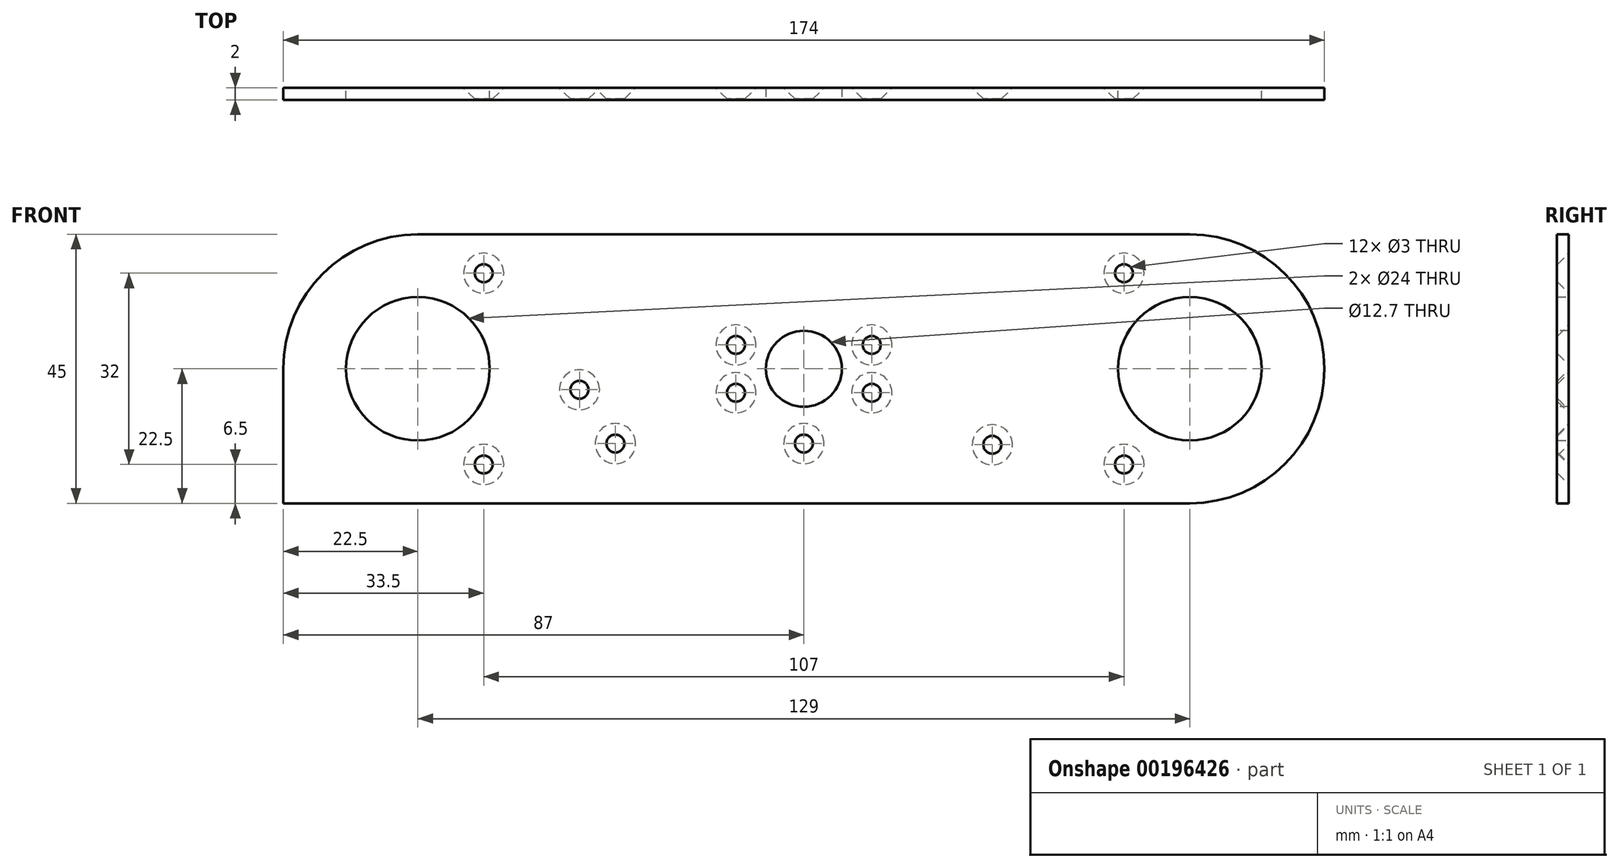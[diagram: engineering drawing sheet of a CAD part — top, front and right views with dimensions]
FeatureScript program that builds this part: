
annotation { "Feature Type Name" : "Feature", "Feature Type Description" : "" }
export const myFeature = defineFeature(function(context is Context, id is Id, definition is map)
    precondition{}
    {
        {
            var Q0;
            Q0=qCreatedBy(makeId("Front.planeOp"),FACE);
            var sketch = newSketch(context, id + "F0", { "sketchPlane" : qUnion([Q0])});
            skLineSegment(sketch, "E0.bottom", {"start": v(64.5, 22.5) * mm, "end": v(-64.5, 22.5) * mm});
            skLineSegment(sketch, "E0.top", {"start": v(64.5, -22.5) * mm, "end": v(-64.5, -22.5) * mm});
            skPoint(sketch, "E0.middle", {"position": v(0, 0) * mm});
            skCircle(sketch, "E1", {"center": v(64.5, 0) * mm, "radius": 12 * mm});
            skCircle(sketch, "E2", {"center": v(-64.5, 0) * mm, "radius": 12 * mm});
            skArc(sketch, "E3", {"start": v(-64.5, 22.5) * mm, "mid": v(-87, 0) * mm, "end": v(-64.5, -22.5) * mm});
            skArc(sketch, "E4", {"start": v(64.5, -22.5) * mm, "mid": v(87, 0) * mm, "end": v(64.5, 22.5) * mm});
            skPoint(sketch, "E5.orphan", {"position": v(-81.5, 22.5) * mm});
            skPoint(sketch, "E6.orphan", {"position": v(-81.5, -22.5) * mm});
            skPoint(sketch, "E7.orphan", {"position": v(81.5, 22.5) * mm});
            skPoint(sketch, "E8.orphan", {"position": v(81.5, -22.5) * mm});
            skSolve(sketch);
        }
        {
            var Q0;
            Q0=qSketchRegion(id+"F0",true);
            extrude(context, id + "F1", {"entities" : qUnion([Q0]), "depth" : 2 * mm, "offsetDistance" : 25 * mm});
        }
        {
            var Q0;
            Q0=makeQuery(id+"F1.opExtrude","CAP_FACE",FACE,{"disambiguationData":[OSD([sQuery(id+"F0.wireOp",EDGE,"E0.bottom"),sQuery(id+"F0.wireOp",EDGE,"E0.top"),sQuery(id+"F0.wireOp",EDGE,"E1"),sQuery(id+"F0.wireOp",EDGE,"E2"),sQuery(id+"F0.wireOp",EDGE,"E3"),sQuery(id+"F0.wireOp",EDGE,"E4")])],"isStart":false});
            var sketch = newSketch(context, id + "F2", { "sketchPlane" : qUnion([Q0])});
            skLineSegment(sketch, "E9.top", {"start": v(-64.5, -22.5) * mm, "end": v(-87, -22.5) * mm});
            skLineSegment(sketch, "E9.right", {"start": v(-87, 0) * mm, "end": v(-87, -22.5) * mm});
            skPoint(sketch, "E9.left.start.orphan", {"position": v(-64.5, 0) * mm});
            skLineSegment(sketch, "E10", {"start": v(-87, 0) * mm, "end": v(-80.88, 0) * mm});
            skLineSegment(sketch, "E11", {"start": v(-80.88, 0) * mm, "end": v(-78.27, -9.46) * mm});
            skLineSegment(sketch, "E12", {"start": v(-78.27, -9.46) * mm, "end": v(-70.55, -14.76) * mm});
            skLineSegment(sketch, "E13", {"start": v(-70.55, -14.76) * mm, "end": v(-64.5, -17.43) * mm});
            skLineSegment(sketch, "E14", {"start": v(-64.5, -17.43) * mm, "end": v(-64.5, -22.5) * mm});
            skSolve(sketch);
        }
        {
            var Q0;
            Q0=qSketchRegion(id+"F2",true);
            extrude(context, id + "F3", {"entities" : qUnion([Q0]), "operationType" : NewBodyOperationType.ADD, "oppositeDirection" : true, "depth" : 2 * mm, "offsetDistance" : 25 * mm});
        }
        {
            var Q0;
            Q0=makeQuery(id+"F3.boolean.opBoolean","MERGE",FACE,{"derivedFrom":[makeQuery(id+"F1.opExtrude","CAP_FACE",FACE,{"disambiguationData":[OSD([sQuery(id+"F0.wireOp",EDGE,"E0.bottom"),sQuery(id+"F0.wireOp",EDGE,"E0.top"),sQuery(id+"F0.wireOp",EDGE,"E1"),sQuery(id+"F0.wireOp",EDGE,"E2"),sQuery(id+"F0.wireOp",EDGE,"E3"),sQuery(id+"F0.wireOp",EDGE,"E4")])],"isStart":false}),makeQuery(id+"F3.opExtrude","CAP_FACE",FACE,{"disambiguationData":[OSD([sQuery(id+"F2.wireOp",EDGE,"E9.top"),sQuery(id+"F2.wireOp",EDGE,"E9.right"),sQuery(id+"F2.wireOp",EDGE,"E10"),sQuery(id+"F2.wireOp",EDGE,"E11"),sQuery(id+"F2.wireOp",EDGE,"E12"),sQuery(id+"F2.wireOp",EDGE,"E13"),sQuery(id+"F2.wireOp",EDGE,"E14")])],"isStart":true})]});
            var sketch = newSketch(context, id + "F4", { "sketchPlane" : qUnion([Q0])});
            skLineSegment(sketch, "E15.bottom", {"start": v(47, 22.5) * mm, "end": v(-47, 22.5) * mm, "construction": true});
            skLineSegment(sketch, "E15.top", {"start": v(47, -22.5) * mm, "end": v(-47, -22.5) * mm, "construction": true});
            skLineSegment(sketch, "E15.left", {"start": v(47, 22.5) * mm, "end": v(47, -22.5) * mm, "construction": true});
            skLineSegment(sketch, "E15.right", {"start": v(-47, 22.5) * mm, "end": v(-47, -22.5) * mm, "construction": true});
            skPoint(sketch, "E15.middle", {"position": v(0, 0) * mm});
            skLineSegment(sketch, "E16", {"start": v(-52.5, 0) * mm, "end": v(52.5, 0) * mm, "construction": true});
            skCircle(sketch, "E17", {"center": v(-53.5, 16) * mm, "radius": 1.5 * mm});
            skCircle(sketch, "E18", {"center": v(-53.5, -16) * mm, "radius": 1.5 * mm});
            skCircle(sketch, "E19", {"center": v(53.5, 16) * mm, "radius": 1.5 * mm});
            skCircle(sketch, "E20", {"center": v(53.5, -16) * mm, "radius": 1.5 * mm});
            skSolve(sketch);
        }
        {
            var Q0;
            Q0=qSketchRegion(id+"F4",true);
            extrude(context, id + "F5", {"entities" : qUnion([Q0]), "operationType" : NewBodyOperationType.REMOVE, "oppositeDirection" : true, "depth" : 25 * mm});
        }
        {
            var Q0;
            Q0=makeQuery(id+"F3.boolean.opBoolean","MERGE",FACE,{"derivedFrom":[makeQuery(id+"F1.opExtrude","CAP_FACE",FACE,{"disambiguationData":[OSD([sQuery(id+"F0.wireOp",EDGE,"E0.bottom"),sQuery(id+"F0.wireOp",EDGE,"E0.top"),sQuery(id+"F0.wireOp",EDGE,"E1"),sQuery(id+"F0.wireOp",EDGE,"E2"),sQuery(id+"F0.wireOp",EDGE,"E3"),sQuery(id+"F0.wireOp",EDGE,"E4")])],"isStart":false}),makeQuery(id+"F3.opExtrude","CAP_FACE",FACE,{"disambiguationData":[OSD([sQuery(id+"F2.wireOp",EDGE,"E9.top"),sQuery(id+"F2.wireOp",EDGE,"E9.right"),sQuery(id+"F2.wireOp",EDGE,"E10"),sQuery(id+"F2.wireOp",EDGE,"E11"),sQuery(id+"F2.wireOp",EDGE,"E12"),sQuery(id+"F2.wireOp",EDGE,"E13"),sQuery(id+"F2.wireOp",EDGE,"E14")])],"isStart":true})]});
            var sketch = newSketch(context, id + "F6", { "sketchPlane" : qUnion([Q0])});
            skCircle(sketch, "E21", {"center": v(0, 0) * mm, "radius": 6.35 * mm});
            skSolve(sketch);
        }
        {
            var Q0;
            Q0=qSketchRegion(id+"F6",true);
            extrude(context, id + "F7", {"entities" : qUnion([Q0]), "operationType" : NewBodyOperationType.REMOVE, "oppositeDirection" : true, "depth" : 25 * mm});
        }
        {
            var Q0;
            Q0=makeQuery(id+"F3.boolean.opBoolean","MERGE",FACE,{"derivedFrom":[makeQuery(id+"F1.opExtrude","CAP_FACE",FACE,{"disambiguationData":[OSD([sQuery(id+"F0.wireOp",EDGE,"E0.bottom"),sQuery(id+"F0.wireOp",EDGE,"E0.top"),sQuery(id+"F0.wireOp",EDGE,"E1"),sQuery(id+"F0.wireOp",EDGE,"E2"),sQuery(id+"F0.wireOp",EDGE,"E3"),sQuery(id+"F0.wireOp",EDGE,"E4")])],"isStart":false}),makeQuery(id+"F3.opExtrude","CAP_FACE",FACE,{"disambiguationData":[OSD([sQuery(id+"F2.wireOp",EDGE,"E9.top"),sQuery(id+"F2.wireOp",EDGE,"E9.right"),sQuery(id+"F2.wireOp",EDGE,"E10"),sQuery(id+"F2.wireOp",EDGE,"E11"),sQuery(id+"F2.wireOp",EDGE,"E12"),sQuery(id+"F2.wireOp",EDGE,"E13"),sQuery(id+"F2.wireOp",EDGE,"E14")])],"isStart":true})]});
            var sketch = newSketch(context, id + "F8", { "sketchPlane" : qUnion([Q0])});
            skPoint(sketch, "E22.middle", {"position": v(0, 0) * mm});
            skCircle(sketch, "E23", {"center": v(-11.35, 4) * mm, "radius": 1.5 * mm});
            skCircle(sketch, "E24", {"center": v(-11.35, -4) * mm, "radius": 1.5 * mm});
            skCircle(sketch, "E25", {"center": v(11.35, 4) * mm, "radius": 1.5 * mm});
            skCircle(sketch, "E26", {"center": v(11.35, -4) * mm, "radius": 1.5 * mm});
            skPoint(sketch, "E27.orphan", {"position": v(-11.35, 11.35) * mm});
            skPoint(sketch, "E28.orphan", {"position": v(11.35, 11.35) * mm});
            skPoint(sketch, "E22.top.start.orphan", {"position": v(11.35, -11.35) * mm});
            skPoint(sketch, "E29.orphan", {"position": v(-11.35, -11.35) * mm});
            skLineSegment(sketch, "E30", {"start": v(52.5, 0) * mm, "end": v(-52.5, 0) * mm, "construction": true});
            skLineSegment(sketch, "E31", {"start": v(-52.5, 0) * mm, "end": v(0, 0) * mm, "construction": true});
            skLineSegment(sketch, "E32", {"start": v(0, 22.5) * mm, "end": v(0, -22.5) * mm, "construction": true});
            skLineSegment(sketch, "E33.bottom", {"start": v(11.35, 11.35) * mm, "end": v(-11.35, 11.35) * mm, "construction": true});
            skLineSegment(sketch, "E33.top", {"start": v(11.35, -11.35) * mm, "end": v(-11.35, -11.35) * mm, "construction": true});
            skLineSegment(sketch, "E33.left", {"start": v(11.35, 11.35) * mm, "end": v(11.35, -11.35) * mm, "construction": true});
            skLineSegment(sketch, "E33.right", {"start": v(-11.35, 11.35) * mm, "end": v(-11.35, -11.35) * mm, "construction": true});
            skSolve(sketch);
        }
        {
            var Q0;
            Q0=qSketchRegion(id+"F8",true);
            extrude(context, id + "F9", {"entities" : qUnion([Q0]), "operationType" : NewBodyOperationType.REMOVE, "oppositeDirection" : true, "depth" : 25 * mm});
        }
        {
            var Q0;
            Q0=makeQuery(id+"F3.boolean.opBoolean","MERGE",FACE,{"derivedFrom":[makeQuery(id+"F1.opExtrude","CAP_FACE",FACE,{"disambiguationData":[OSD([sQuery(id+"F0.wireOp",EDGE,"E0.bottom"),sQuery(id+"F0.wireOp",EDGE,"E0.top"),sQuery(id+"F0.wireOp",EDGE,"E1"),sQuery(id+"F0.wireOp",EDGE,"E2"),sQuery(id+"F0.wireOp",EDGE,"E3"),sQuery(id+"F0.wireOp",EDGE,"E4")])],"isStart":false}),makeQuery(id+"F3.opExtrude","CAP_FACE",FACE,{"disambiguationData":[OSD([sQuery(id+"F2.wireOp",EDGE,"E9.top"),sQuery(id+"F2.wireOp",EDGE,"E9.right"),sQuery(id+"F2.wireOp",EDGE,"E10"),sQuery(id+"F2.wireOp",EDGE,"E11"),sQuery(id+"F2.wireOp",EDGE,"E12"),sQuery(id+"F2.wireOp",EDGE,"E13"),sQuery(id+"F2.wireOp",EDGE,"E14")])],"isStart":true})]});
            var sketch = newSketch(context, id + "F10", { "sketchPlane" : qUnion([Q0])});
            skCircle(sketch, "E34", {"center": v(0, -12.5) * mm, "radius": 1.5 * mm});
            skCircle(sketch, "E35", {"center": v(31.5, -12.7) * mm, "radius": 1.5 * mm});
            skCircle(sketch, "E36", {"center": v(-31.5, -12.5) * mm, "radius": 1.5 * mm});
            skLineSegment(sketch, "E37", {"start": v(-31.5, -12.5) * mm, "end": v(-43.5, -12.5) * mm, "construction": true});
            skLineSegment(sketch, "E38", {"start": v(-37.5, -12.5) * mm, "end": v(-37.5, -3.5) * mm, "construction": true});
            skCircle(sketch, "E39", {"center": v(-37.5, -3.5) * mm, "radius": 1.5 * mm});
            skSolve(sketch);
        }
        {
            var Q0;
            Q0 = qSketchRegion(id + "F10", true);
            extrude(context, id + "F11", {"entities" : qUnion([Q0]), "operationType" : NewBodyOperationType.REMOVE, "oppositeDirection" : true, "depth" : 25 * mm});
        }
        {
            var Q0;
            Q0=makeQuery(id+"F5.boolean.opBoolean","INTERSECT",EDGE,{"derivedFrom":[makeQuery(id+"F3.boolean.opBoolean","MERGE",FACE,{"derivedFrom":[makeQuery(id+"F1.opExtrude","CAP_FACE",FACE,{"disambiguationData":[OSD([sQuery(id+"F0.wireOp",EDGE,"E0.bottom"),sQuery(id+"F0.wireOp",EDGE,"E0.top"),sQuery(id+"F0.wireOp",EDGE,"E1"),sQuery(id+"F0.wireOp",EDGE,"E2"),sQuery(id+"F0.wireOp",EDGE,"E3"),sQuery(id+"F0.wireOp",EDGE,"E4")])],"isStart":true}),makeQuery(id+"F3.opExtrude","CAP_FACE",FACE,{"disambiguationData":[OSD([sQuery(id+"F2.wireOp",EDGE,"E9.top"),sQuery(id+"F2.wireOp",EDGE,"E9.right"),sQuery(id+"F2.wireOp",EDGE,"E10"),sQuery(id+"F2.wireOp",EDGE,"E11"),sQuery(id+"F2.wireOp",EDGE,"E12"),sQuery(id+"F2.wireOp",EDGE,"E13"),sQuery(id+"F2.wireOp",EDGE,"E14")])],"isStart":false})]}),makeQuery(id+"F5.opExtrude","SWEPT_FACE",FACE,{"disambiguationData":[OSD([sQuery(id+"F4.wireOp",EDGE,"E18")])]})]});
            var Q1;
            Q1=makeQuery(id+"F11.boolean.opBoolean","INTERSECT",EDGE,{"derivedFrom":[makeQuery(id+"F3.boolean.opBoolean","MERGE",FACE,{"derivedFrom":[makeQuery(id+"F1.opExtrude","CAP_FACE",FACE,{"disambiguationData":[OSD([sQuery(id+"F0.wireOp",EDGE,"E0.bottom"),sQuery(id+"F0.wireOp",EDGE,"E0.top"),sQuery(id+"F0.wireOp",EDGE,"E1"),sQuery(id+"F0.wireOp",EDGE,"E2"),sQuery(id+"F0.wireOp",EDGE,"E3"),sQuery(id+"F0.wireOp",EDGE,"E4")])],"isStart":true}),makeQuery(id+"F3.opExtrude","CAP_FACE",FACE,{"disambiguationData":[OSD([sQuery(id+"F2.wireOp",EDGE,"E9.top"),sQuery(id+"F2.wireOp",EDGE,"E9.right"),sQuery(id+"F2.wireOp",EDGE,"E10"),sQuery(id+"F2.wireOp",EDGE,"E11"),sQuery(id+"F2.wireOp",EDGE,"E12"),sQuery(id+"F2.wireOp",EDGE,"E13"),sQuery(id+"F2.wireOp",EDGE,"E14")])],"isStart":false})]}),makeQuery(id+"F11.opExtrude","SWEPT_FACE",FACE,{"disambiguationData":[OSD([sQuery(id+"F10.wireOp",EDGE,"E36")])]})]});
            var Q2;
            Q2=makeQuery(id+"F5.boolean.opBoolean","INTERSECT",EDGE,{"derivedFrom":[makeQuery(id+"F3.boolean.opBoolean","MERGE",FACE,{"derivedFrom":[makeQuery(id+"F1.opExtrude","CAP_FACE",FACE,{"disambiguationData":[OSD([sQuery(id+"F0.wireOp",EDGE,"E0.bottom"),sQuery(id+"F0.wireOp",EDGE,"E0.top"),sQuery(id+"F0.wireOp",EDGE,"E1"),sQuery(id+"F0.wireOp",EDGE,"E2"),sQuery(id+"F0.wireOp",EDGE,"E3"),sQuery(id+"F0.wireOp",EDGE,"E4")])],"isStart":true}),makeQuery(id+"F3.opExtrude","CAP_FACE",FACE,{"disambiguationData":[OSD([sQuery(id+"F2.wireOp",EDGE,"E9.top"),sQuery(id+"F2.wireOp",EDGE,"E9.right"),sQuery(id+"F2.wireOp",EDGE,"E10"),sQuery(id+"F2.wireOp",EDGE,"E11"),sQuery(id+"F2.wireOp",EDGE,"E12"),sQuery(id+"F2.wireOp",EDGE,"E13"),sQuery(id+"F2.wireOp",EDGE,"E14")])],"isStart":false})]}),makeQuery(id+"F5.opExtrude","SWEPT_FACE",FACE,{"disambiguationData":[OSD([sQuery(id+"F4.wireOp",EDGE,"E17")])]})]});
            var Q3;
            Q3=makeQuery(id+"F9.boolean.opBoolean","INTERSECT",EDGE,{"derivedFrom":[makeQuery(id+"F3.boolean.opBoolean","MERGE",FACE,{"derivedFrom":[makeQuery(id+"F1.opExtrude","CAP_FACE",FACE,{"disambiguationData":[OSD([sQuery(id+"F0.wireOp",EDGE,"E0.bottom"),sQuery(id+"F0.wireOp",EDGE,"E0.top"),sQuery(id+"F0.wireOp",EDGE,"E1"),sQuery(id+"F0.wireOp",EDGE,"E2"),sQuery(id+"F0.wireOp",EDGE,"E3"),sQuery(id+"F0.wireOp",EDGE,"E4")])],"isStart":true}),makeQuery(id+"F3.opExtrude","CAP_FACE",FACE,{"disambiguationData":[OSD([sQuery(id+"F2.wireOp",EDGE,"E9.top"),sQuery(id+"F2.wireOp",EDGE,"E9.right"),sQuery(id+"F2.wireOp",EDGE,"E10"),sQuery(id+"F2.wireOp",EDGE,"E11"),sQuery(id+"F2.wireOp",EDGE,"E12"),sQuery(id+"F2.wireOp",EDGE,"E13"),sQuery(id+"F2.wireOp",EDGE,"E14")])],"isStart":false})]}),makeQuery(id+"F9.opExtrude","SWEPT_FACE",FACE,{"disambiguationData":[OSD([sQuery(id+"F8.wireOp",EDGE,"E24")])]})]});
            var Q4;
            Q4=makeQuery(id+"F9.boolean.opBoolean","INTERSECT",EDGE,{"derivedFrom":[makeQuery(id+"F3.boolean.opBoolean","MERGE",FACE,{"derivedFrom":[makeQuery(id+"F1.opExtrude","CAP_FACE",FACE,{"disambiguationData":[OSD([sQuery(id+"F0.wireOp",EDGE,"E0.bottom"),sQuery(id+"F0.wireOp",EDGE,"E0.top"),sQuery(id+"F0.wireOp",EDGE,"E1"),sQuery(id+"F0.wireOp",EDGE,"E2"),sQuery(id+"F0.wireOp",EDGE,"E3"),sQuery(id+"F0.wireOp",EDGE,"E4")])],"isStart":true}),makeQuery(id+"F3.opExtrude","CAP_FACE",FACE,{"disambiguationData":[OSD([sQuery(id+"F2.wireOp",EDGE,"E9.top"),sQuery(id+"F2.wireOp",EDGE,"E9.right"),sQuery(id+"F2.wireOp",EDGE,"E10"),sQuery(id+"F2.wireOp",EDGE,"E11"),sQuery(id+"F2.wireOp",EDGE,"E12"),sQuery(id+"F2.wireOp",EDGE,"E13"),sQuery(id+"F2.wireOp",EDGE,"E14")])],"isStart":false})]}),makeQuery(id+"F9.opExtrude","SWEPT_FACE",FACE,{"disambiguationData":[OSD([sQuery(id+"F8.wireOp",EDGE,"E23")])]})]});
            var Q5;
            Q5=makeQuery(id+"F11.boolean.opBoolean","INTERSECT",EDGE,{"derivedFrom":[makeQuery(id+"F3.boolean.opBoolean","MERGE",FACE,{"derivedFrom":[makeQuery(id+"F1.opExtrude","CAP_FACE",FACE,{"disambiguationData":[OSD([sQuery(id+"F0.wireOp",EDGE,"E0.bottom"),sQuery(id+"F0.wireOp",EDGE,"E0.top"),sQuery(id+"F0.wireOp",EDGE,"E1"),sQuery(id+"F0.wireOp",EDGE,"E2"),sQuery(id+"F0.wireOp",EDGE,"E3"),sQuery(id+"F0.wireOp",EDGE,"E4")])],"isStart":true}),makeQuery(id+"F3.opExtrude","CAP_FACE",FACE,{"disambiguationData":[OSD([sQuery(id+"F2.wireOp",EDGE,"E9.top"),sQuery(id+"F2.wireOp",EDGE,"E9.right"),sQuery(id+"F2.wireOp",EDGE,"E10"),sQuery(id+"F2.wireOp",EDGE,"E11"),sQuery(id+"F2.wireOp",EDGE,"E12"),sQuery(id+"F2.wireOp",EDGE,"E13"),sQuery(id+"F2.wireOp",EDGE,"E14")])],"isStart":false})]}),makeQuery(id+"F11.opExtrude","SWEPT_FACE",FACE,{"disambiguationData":[OSD([sQuery(id+"F10.wireOp",EDGE,"E34")])]})]});
            var Q6;
            Q6=makeQuery(id+"F9.boolean.opBoolean","INTERSECT",EDGE,{"derivedFrom":[makeQuery(id+"F3.boolean.opBoolean","MERGE",FACE,{"derivedFrom":[makeQuery(id+"F1.opExtrude","CAP_FACE",FACE,{"disambiguationData":[OSD([sQuery(id+"F0.wireOp",EDGE,"E0.bottom"),sQuery(id+"F0.wireOp",EDGE,"E0.top"),sQuery(id+"F0.wireOp",EDGE,"E1"),sQuery(id+"F0.wireOp",EDGE,"E2"),sQuery(id+"F0.wireOp",EDGE,"E3"),sQuery(id+"F0.wireOp",EDGE,"E4")])],"isStart":true}),makeQuery(id+"F3.opExtrude","CAP_FACE",FACE,{"disambiguationData":[OSD([sQuery(id+"F2.wireOp",EDGE,"E9.top"),sQuery(id+"F2.wireOp",EDGE,"E9.right"),sQuery(id+"F2.wireOp",EDGE,"E10"),sQuery(id+"F2.wireOp",EDGE,"E11"),sQuery(id+"F2.wireOp",EDGE,"E12"),sQuery(id+"F2.wireOp",EDGE,"E13"),sQuery(id+"F2.wireOp",EDGE,"E14")])],"isStart":false})]}),makeQuery(id+"F9.opExtrude","SWEPT_FACE",FACE,{"disambiguationData":[OSD([sQuery(id+"F8.wireOp",EDGE,"E26")])]})]});
            var Q7;
            Q7=makeQuery(id+"F9.boolean.opBoolean","INTERSECT",EDGE,{"derivedFrom":[makeQuery(id+"F3.boolean.opBoolean","MERGE",FACE,{"derivedFrom":[makeQuery(id+"F1.opExtrude","CAP_FACE",FACE,{"disambiguationData":[OSD([sQuery(id+"F0.wireOp",EDGE,"E0.bottom"),sQuery(id+"F0.wireOp",EDGE,"E0.top"),sQuery(id+"F0.wireOp",EDGE,"E1"),sQuery(id+"F0.wireOp",EDGE,"E2"),sQuery(id+"F0.wireOp",EDGE,"E3"),sQuery(id+"F0.wireOp",EDGE,"E4")])],"isStart":true}),makeQuery(id+"F3.opExtrude","CAP_FACE",FACE,{"disambiguationData":[OSD([sQuery(id+"F2.wireOp",EDGE,"E9.top"),sQuery(id+"F2.wireOp",EDGE,"E9.right"),sQuery(id+"F2.wireOp",EDGE,"E10"),sQuery(id+"F2.wireOp",EDGE,"E11"),sQuery(id+"F2.wireOp",EDGE,"E12"),sQuery(id+"F2.wireOp",EDGE,"E13"),sQuery(id+"F2.wireOp",EDGE,"E14")])],"isStart":false})]}),makeQuery(id+"F9.opExtrude","SWEPT_FACE",FACE,{"disambiguationData":[OSD([sQuery(id+"F8.wireOp",EDGE,"E25")])]})]});
            var Q8;
            Q8=makeQuery(id+"F11.boolean.opBoolean","INTERSECT",EDGE,{"derivedFrom":[makeQuery(id+"F3.boolean.opBoolean","MERGE",FACE,{"derivedFrom":[makeQuery(id+"F1.opExtrude","CAP_FACE",FACE,{"disambiguationData":[OSD([sQuery(id+"F0.wireOp",EDGE,"E0.bottom"),sQuery(id+"F0.wireOp",EDGE,"E0.top"),sQuery(id+"F0.wireOp",EDGE,"E1"),sQuery(id+"F0.wireOp",EDGE,"E2"),sQuery(id+"F0.wireOp",EDGE,"E3"),sQuery(id+"F0.wireOp",EDGE,"E4")])],"isStart":true}),makeQuery(id+"F3.opExtrude","CAP_FACE",FACE,{"disambiguationData":[OSD([sQuery(id+"F2.wireOp",EDGE,"E9.top"),sQuery(id+"F2.wireOp",EDGE,"E9.right"),sQuery(id+"F2.wireOp",EDGE,"E10"),sQuery(id+"F2.wireOp",EDGE,"E11"),sQuery(id+"F2.wireOp",EDGE,"E12"),sQuery(id+"F2.wireOp",EDGE,"E13"),sQuery(id+"F2.wireOp",EDGE,"E14")])],"isStart":false})]}),makeQuery(id+"F11.opExtrude","SWEPT_FACE",FACE,{"disambiguationData":[OSD([sQuery(id+"F10.wireOp",EDGE,"E35")])]})]});
            var Q9;
            Q9=makeQuery(id+"F5.boolean.opBoolean","INTERSECT",EDGE,{"derivedFrom":[makeQuery(id+"F3.boolean.opBoolean","MERGE",FACE,{"derivedFrom":[makeQuery(id+"F1.opExtrude","CAP_FACE",FACE,{"disambiguationData":[OSD([sQuery(id+"F0.wireOp",EDGE,"E0.bottom"),sQuery(id+"F0.wireOp",EDGE,"E0.top"),sQuery(id+"F0.wireOp",EDGE,"E1"),sQuery(id+"F0.wireOp",EDGE,"E2"),sQuery(id+"F0.wireOp",EDGE,"E3"),sQuery(id+"F0.wireOp",EDGE,"E4")])],"isStart":true}),makeQuery(id+"F3.opExtrude","CAP_FACE",FACE,{"disambiguationData":[OSD([sQuery(id+"F2.wireOp",EDGE,"E9.top"),sQuery(id+"F2.wireOp",EDGE,"E9.right"),sQuery(id+"F2.wireOp",EDGE,"E10"),sQuery(id+"F2.wireOp",EDGE,"E11"),sQuery(id+"F2.wireOp",EDGE,"E12"),sQuery(id+"F2.wireOp",EDGE,"E13"),sQuery(id+"F2.wireOp",EDGE,"E14")])],"isStart":false})]}),makeQuery(id+"F5.opExtrude","SWEPT_FACE",FACE,{"disambiguationData":[OSD([sQuery(id+"F4.wireOp",EDGE,"E20")])]})]});
            var Q10;
            Q10=makeQuery(id+"F5.boolean.opBoolean","INTERSECT",EDGE,{"derivedFrom":[makeQuery(id+"F3.boolean.opBoolean","MERGE",FACE,{"derivedFrom":[makeQuery(id+"F1.opExtrude","CAP_FACE",FACE,{"disambiguationData":[OSD([sQuery(id+"F0.wireOp",EDGE,"E0.bottom"),sQuery(id+"F0.wireOp",EDGE,"E0.top"),sQuery(id+"F0.wireOp",EDGE,"E1"),sQuery(id+"F0.wireOp",EDGE,"E2"),sQuery(id+"F0.wireOp",EDGE,"E3"),sQuery(id+"F0.wireOp",EDGE,"E4")])],"isStart":true}),makeQuery(id+"F3.opExtrude","CAP_FACE",FACE,{"disambiguationData":[OSD([sQuery(id+"F2.wireOp",EDGE,"E9.top"),sQuery(id+"F2.wireOp",EDGE,"E9.right"),sQuery(id+"F2.wireOp",EDGE,"E10"),sQuery(id+"F2.wireOp",EDGE,"E11"),sQuery(id+"F2.wireOp",EDGE,"E12"),sQuery(id+"F2.wireOp",EDGE,"E13"),sQuery(id+"F2.wireOp",EDGE,"E14")])],"isStart":false})]}),makeQuery(id+"F5.opExtrude","SWEPT_FACE",FACE,{"disambiguationData":[OSD([sQuery(id+"F4.wireOp",EDGE,"E19")])]})]});
            var Q11;
            Q11=makeQuery(id+"F11.boolean.opBoolean","INTERSECT",EDGE,{"derivedFrom":[makeQuery(id+"F3.boolean.opBoolean","MERGE",FACE,{"derivedFrom":[makeQuery(id+"F1.opExtrude","CAP_FACE",FACE,{"disambiguationData":[OSD([sQuery(id+"F0.wireOp",EDGE,"E0.bottom"),sQuery(id+"F0.wireOp",EDGE,"E0.top"),sQuery(id+"F0.wireOp",EDGE,"E1"),sQuery(id+"F0.wireOp",EDGE,"E2"),sQuery(id+"F0.wireOp",EDGE,"E3"),sQuery(id+"F0.wireOp",EDGE,"E4")])],"isStart":true}),makeQuery(id+"F3.opExtrude","CAP_FACE",FACE,{"disambiguationData":[OSD([sQuery(id+"F2.wireOp",EDGE,"E9.top"),sQuery(id+"F2.wireOp",EDGE,"E9.right"),sQuery(id+"F2.wireOp",EDGE,"E10"),sQuery(id+"F2.wireOp",EDGE,"E11"),sQuery(id+"F2.wireOp",EDGE,"E12"),sQuery(id+"F2.wireOp",EDGE,"E13"),sQuery(id+"F2.wireOp",EDGE,"E14")])],"isStart":false})]}),makeQuery(id+"F11.opExtrude","SWEPT_FACE",FACE,{"disambiguationData":[OSD([sQuery(id+"F10.wireOp",EDGE,"E39")])]})]});
            chamfer(context, id + "F12", {"entities" : qUnion([Q0, Q1, Q2, Q3, Q4, Q5, Q6, Q7, Q8, Q9, Q10, Q11]), "width" : 1.86 * mm, "tangentPropagation" : true});
        }
    });
